# Revit family: hansgrohe_25036XXX-FixFit-Wall-outlet-square_NEW
name_source: partatom
category: Plumbing Fixtures
revit_build: Autodesk Revit 2015 (Build: 20140903_1530(x64)
units: mm (PartAtom-declared; Revit-internal decimal feet)

## types (2) — shared parameters
Always visible = Yes
Brand url = http://www.hansgrohe-int.com
Design country = Germany
Edition number = 1
GTIN code = https://4059625268988
IFC Classification = Sanitary Terminal
Installation instructions = https://www.hansgrohe.de
Manufacturer country = Germany
Manufacturer name = hansgrohe
Product Guid = 8ff37ea3-f425-48e8-b325-e550ba0b528a
Product SKU = 25036XXX
Product data url = https://bimobject.com
Product family = Fixfit
Product group = Wall outlet
Product name = 25036XXX FixFit Wall outlet square
Product url = https://www.hansgrohe.de
QR code = http://bimobject.com
Technical description = https://www.hansgrohe.de

## per-type parameters (varying)
| type | Material 1 |
| 700 Matt White | Hansgrohe - Fixfit - 700 Matt White |
| 000 Chrome | Hansgrohe - Fixfit - 000 Chrome |

## geometry (parser evidence)
native form markers: Sweep x2
no freeform markers — native parametric forms only
